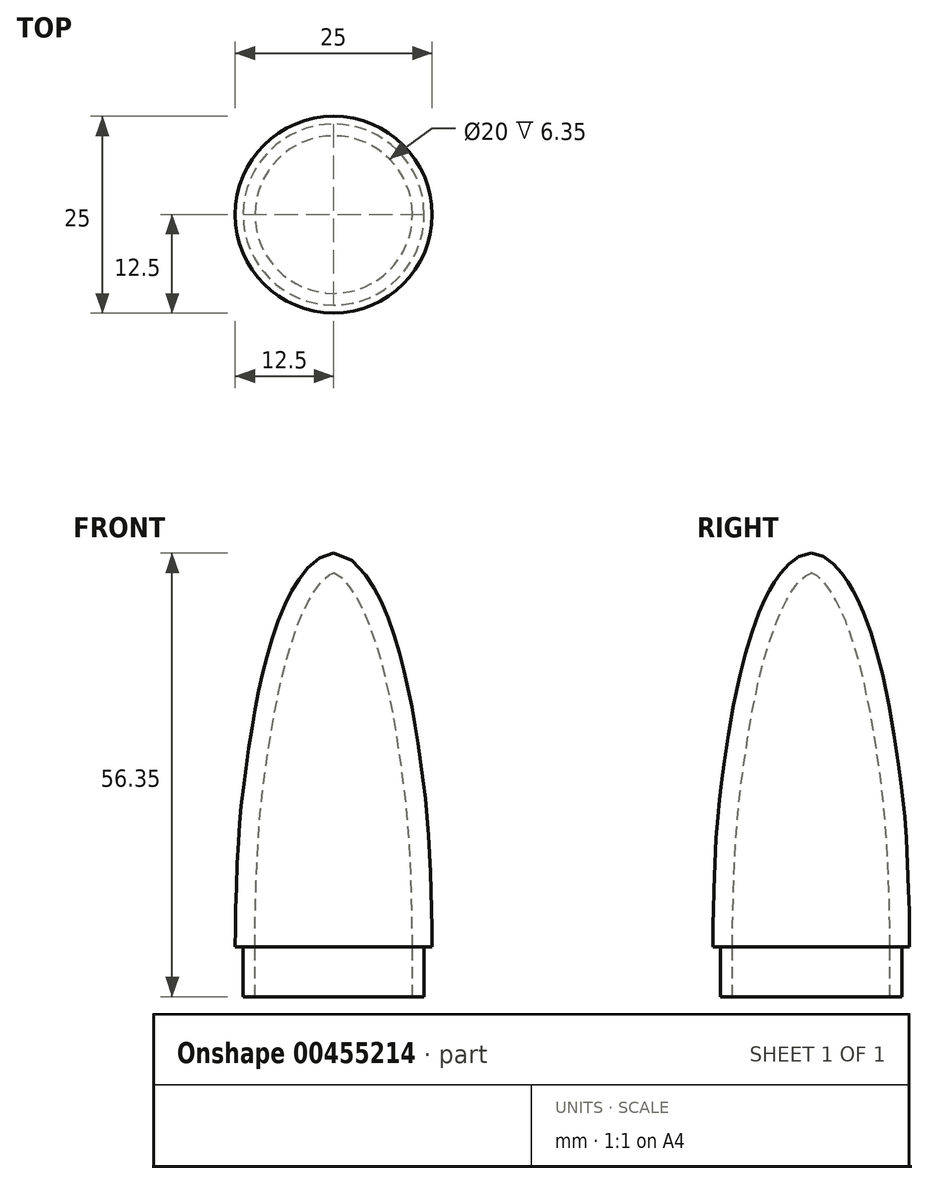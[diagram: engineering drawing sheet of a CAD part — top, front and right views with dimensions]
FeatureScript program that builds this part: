
annotation { "Feature Type Name" : "Feature", "Feature Type Description" : "" }
export const myFeature = defineFeature(function(context is Context, id is Id, definition is map)
    precondition{}
    {
        {
            var Q0;
            Q0=qCreatedBy(makeId("Front.planeOp"),FACE);
            var sketch = newSketch(context, id + "F0", { "sketchPlane" : qUnion([Q0])});
            skLineSegment(sketch, "E0", {"start": v(0, 0) * mm, "end": v(0, 50) * mm});
            skLineSegment(sketch, "E1", {"start": v(0, 0) * mm, "end": v(-12.5, 0) * mm});
            skLineSegment(sketch, "E2", {"start": v(0, 0) * mm, "end": v(12.5, 0) * mm});
            skPoint(sketch, "E3", {"position": v(0, 50) * mm});
            skPoint(sketch, "E4", {"position": v(-1.62, 49.46) * mm});
            skPoint(sketch, "E5", {"position": v(-3.02, 48.44) * mm});
            skPoint(sketch, "E6", {"position": v(-4, 47.28) * mm});
            skPoint(sketch, "E7", {"position": v(-4.82, 46.06) * mm});
            skPoint(sketch, "E8", {"position": v(-5.58, 44.67) * mm});
            skPoint(sketch, "E9", {"position": v(-6.32, 43.21) * mm});
            skPoint(sketch, "E10", {"position": v(-7.25, 40.8) * mm});
            skPoint(sketch, "E11", {"position": v(-8.03, 38.4) * mm});
            skPoint(sketch, "E12", {"position": v(-8.72, 35.88) * mm});
            skPoint(sketch, "E13", {"position": v(-9.2, 33.94) * mm});
            skPoint(sketch, "E14", {"position": v(-9.73, 31.5) * mm});
            skPoint(sketch, "E15", {"position": v(-10.2, 28.92) * mm});
            skPoint(sketch, "E16", {"position": v(-10.63, 26.44) * mm});
            skPoint(sketch, "E17", {"position": v(-11.1, 23.1) * mm});
            skPoint(sketch, "E18", {"position": v(-11.45, 20.28) * mm});
            skPoint(sketch, "E19", {"position": v(-11.75, 17.73) * mm});
            skPoint(sketch, "E20", {"position": v(-11.9, 15.45) * mm});
            skPoint(sketch, "E21", {"position": v(-12.13, 12.84) * mm});
            skPoint(sketch, "E22", {"position": v(-12.34, 8.99) * mm});
            skPoint(sketch, "E23", {"position": v(-12.43, 5.27) * mm});
            skPoint(sketch, "E24", {"position": v(-12.53, 2.45) * mm});
            skPoint(sketch, "E25", {"position": v(-12.5, 0) * mm});
            skPoint(sketch, "E26.MirrorP", {"position": v(1.62, 49.46) * mm});
            skPoint(sketch, "E27.MirrorP", {"position": v(3.02, 48.44) * mm});
            skPoint(sketch, "E28.MirrorP", {"position": v(4, 47.28) * mm});
            skPoint(sketch, "E29.MirrorP", {"position": v(4.82, 46.06) * mm});
            skPoint(sketch, "E30.MirrorP", {"position": v(5.58, 44.67) * mm});
            skPoint(sketch, "E31.MirrorP", {"position": v(6.32, 43.21) * mm});
            skPoint(sketch, "E32.MirrorP", {"position": v(7.25, 40.8) * mm});
            skPoint(sketch, "E33.MirrorP", {"position": v(8.03, 38.4) * mm});
            skPoint(sketch, "E34.MirrorP", {"position": v(8.72, 35.88) * mm});
            skPoint(sketch, "E35.MirrorP", {"position": v(9.2, 33.94) * mm});
            skPoint(sketch, "E36.MirrorP", {"position": v(9.73, 31.5) * mm});
            skPoint(sketch, "E37.MirrorP", {"position": v(10.2, 28.92) * mm});
            skPoint(sketch, "E38.MirrorP", {"position": v(10.63, 26.44) * mm});
            skPoint(sketch, "E39.MirrorP", {"position": v(11.1, 23.1) * mm});
            skPoint(sketch, "E40.MirrorP", {"position": v(11.45, 20.28) * mm});
            skPoint(sketch, "E41.MirrorP", {"position": v(11.75, 17.73) * mm});
            skPoint(sketch, "E42.MirrorP", {"position": v(11.9, 15.45) * mm});
            skPoint(sketch, "E43.MirrorP", {"position": v(12.13, 12.84) * mm});
            skPoint(sketch, "E44.MirrorP", {"position": v(12.34, 8.99) * mm});
            skPoint(sketch, "E45.MirrorP", {"position": v(12.43, 5.27) * mm});
            skPoint(sketch, "E46.MirrorP", {"position": v(12.53, 2.45) * mm});
            skPoint(sketch, "E47.MirrorP", {"position": v(12.5, 0) * mm});
            skFitSpline(sketch, "E48", {"points": [v(-12.5, 0) * mm, v(-12.43, 5.27) * mm, v(-12.13, 12.84) * mm, v(-11.75, 17.73) * mm, v(-11.1, 23.1) * mm, v(-10.2, 28.92) * mm, v(-9.2, 33.94) * mm, v(-8.03, 38.4) * mm, v(-6.32, 43.21) * mm, v(-4.82, 46.06) * mm, v(-3.02, 48.44) * mm, v(0, 50) * mm, v(3.02, 48.44) * mm, v(4.82, 46.06) * mm, v(6.32, 43.21) * mm, v(8.03, 38.4) * mm, v(9.2, 33.94) * mm, v(10.2, 28.92) * mm, v(11.1, 23.1) * mm, v(11.75, 17.73) * mm, v(12.13, 12.84) * mm, v(12.43, 5.27) * mm, v(12.5, 0) * mm], "startDerivative": vector(0.56, 103.04) * mm, "endDerivative": vector(0.56, -103.04) * mm});
            skSolve(sketch);
        }
        {
            var Q0;
            {var subQ0=sQuery(id+"F0.wireOp",EDGE,"E0");Q0=makeQuery(id+"F0.imprint","IMPRINT",FACE,{"disambiguationData":[TD([[makeQuery(id+"F0.imprint","IMPRINT",EDGE,{"derivedFrom":subQ0}),1.0]])]});}
            var Q1;
            Q1=sQuery(id+"F0.wireOp",EDGE,"E0");
            revolve(context, id + "F1", {"entities" : qUnion([Q0]), "axis" : qUnion([Q1]), "revolveType" : RevolveType.FULL});
        }
        {
            var Q0;
            Q0=makeQuery(id+"F1.opRevolve","SWEPT_FACE",FACE,{"disambiguationData":[OSD([sQuery(id+"F0.wireOp",EDGE,"E1")])]});
            shell(context, id + "F2", {"entities" : qUnion([Q0]), "thickness" : 2.5 * mm});
        }
        {
            var Q0;
            Q0=makeQuery(id+"F1.opRevolve","SWEPT_FACE",FACE,{"disambiguationData":[OSD([sQuery(id+"F0.wireOp",EDGE,"E1")])]});
            var sketch = newSketch(context, id + "F3", { "sketchPlane" : qUnion([Q0])});
            skCircle(sketch, "E49", {"center": v(0, 0) * mm, "radius": 11.5 * mm});
            skSolve(sketch);
        }
        {
            var Q0;
            Q0=makeQuery(id+"F3.imprint","IMPRINT",FACE,{"disambiguationData":[TD([[makeQuery(id+"F3.imprint","IMPRINT",EDGE,{"derivedFrom":sQuery(id+"F3.wireOp",EDGE,"E49")}),1.0]])]});
            extrude(context, id + "F4", {"entities" : qUnion([Q0]), "operationType" : NewBodyOperationType.ADD, "depth" : 6.35 * mm, "offsetDistance" : 25 * mm});
        }
    });
